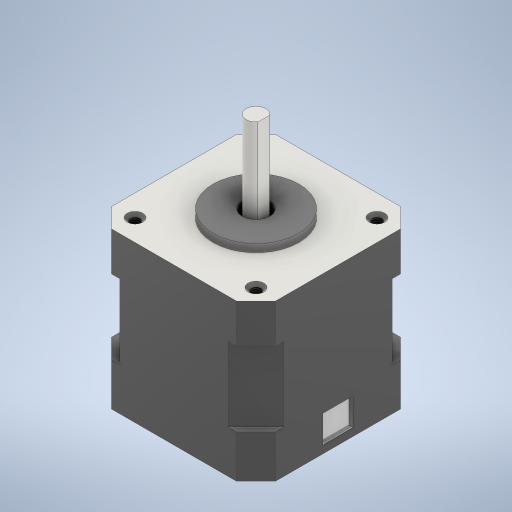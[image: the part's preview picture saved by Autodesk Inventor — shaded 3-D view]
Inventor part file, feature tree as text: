
AUTODESK INVENTOR PART (.ipt)
format: ipt  version: 2023 (Build 270158000, 158)  size: 352,768 bytes
history: native  units: in
note: dims shown in document units (in); Inventor stores cm internally (conversion verified against a paired STEP export)
features: extrude x8, sketch x5, projected_geometry x5, plane x2, hole x1, chamfer x1
ambient origin geometry x8: Origin, YZ Plane, XZ Plane, XY Plane, X Axis, Y Axis, Z Axis, Center Point
bodies: Body1 (feature_tree)
feature tree (22):
  sketch  "Sketch2"  dims[d15=1.6535in d16=1.6535in]
  extrude  "Extrusion3"  Depth=1.6535in
  extrude  "Extrusion4"  Depth=0.2756in
  hole  "Hole1"  [1 undecoded]
  chamfer  "Chamfer1"  Distance=0.0787in
  plane  "Work Plane1"
  extrude  "Extrusion5"  Depth=0.0787in TaperAngle=45.0deg
  plane  "Work Plane2"
  extrude  "Extrusion6"  TaperAngle=0.0deg  [1 undecoded]
  extrude  "Extrusion7"  Depth=0.0591in
  extrude  "Extrusion8"  Depth=0.0591in
  extrude  "Extrusion9"  Depth=0.3937in TaperAngle=0.0deg
  extrude  "Extrusion10"  Depth=0.3937in TaperAngle=0.0deg
  sketch  "Sketch3"  dims[d17=0.8661in d18=0.2756in]
  projected_geometry  "Projected Loop1"
  projected_geometry  "Projected Loop2"
  sketch  "Sketch4"  dims[d19=0.1969in d20=1.5748in d21=0.0in d22=0.0787in d23=0.0in]
  projected_geometry  "Projected Loop3"
  projected_geometry  "Projected Loop4"
  sketch  "Sketch5"  dims[d24=0.0968in d25=0.1772in d26=0.1575in d27=0.0787in d28=90.0deg d29=0.1772in d30=0.8108in d31=0.1969in d32=0.0787in d33=45.0deg]
  projected_geometry  "Projected Loop5"
  sketch  "Sketch6"  dims[d36=0.0591in d37=0.0in d38=0.0in d39=0.0591in d40=0.0591in d41=0.3937in d42=0.0in d43=0.3937in d44=0.0in d45=0.9055in d46=0.0in d47=0.1772in d48=0.0in d49=0.0in d50=0.0591in d51=0.3031in d52=0.2756in d53=0.0394in d54=0.0in]
note: 2 required parameter values undecoded (feature->parameter linkage not recoverable at this tier; creation-order binding heuristic only, values carry confidence <= 0.55)
